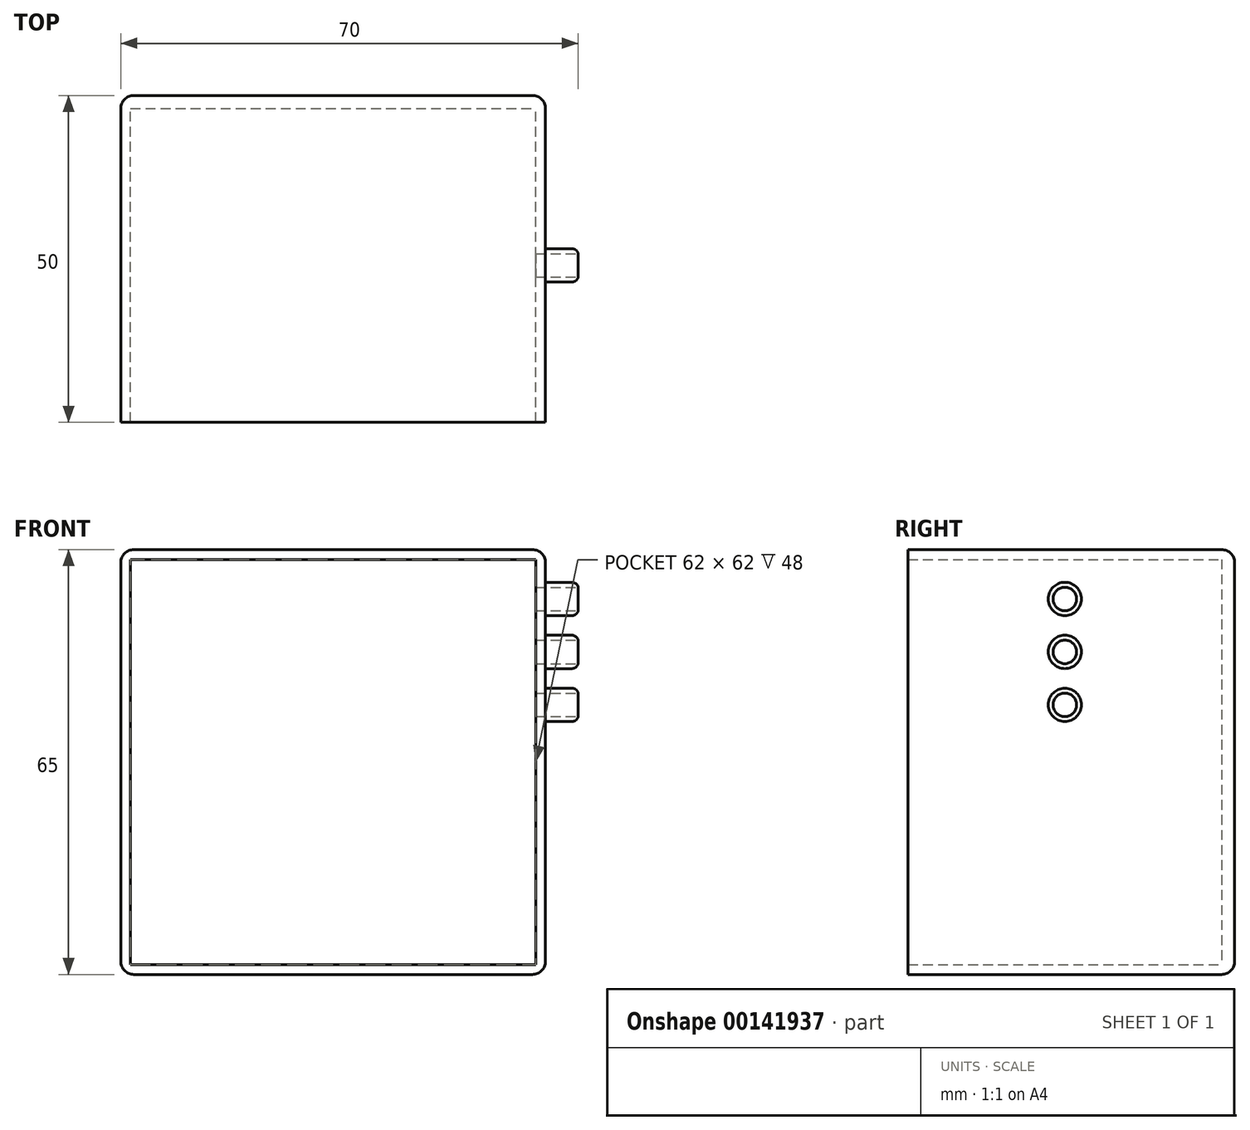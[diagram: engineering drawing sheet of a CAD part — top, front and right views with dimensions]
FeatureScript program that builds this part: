
annotation { "Feature Type Name" : "Feature", "Feature Type Description" : "" }
export const myFeature = defineFeature(function(context is Context, id is Id, definition is map)
    precondition{}
    {
        {
            var Q0;
            Q0=qCreatedBy(makeId("Front.planeOp"),FACE);
            var sketch = newSketch(context, id + "F0", { "sketchPlane" : qUnion([Q0])});
            skLineSegment(sketch, "E0.bottom", {"start": v(-31.66, 27.38) * mm, "end": v(30.34, 27.38) * mm});
            skLineSegment(sketch, "E0.top", {"start": v(-31.66, -34.62) * mm, "end": v(30.34, -34.62) * mm});
            skLineSegment(sketch, "E0.left", {"start": v(-31.66, 27.38) * mm, "end": v(-31.66, -34.62) * mm});
            skLineSegment(sketch, "E0.right", {"start": v(30.34, 27.38) * mm, "end": v(30.34, -34.62) * mm});
            skLineSegment(sketch, "E1.bottom", {"start": v(-33.16, 28.88) * mm, "end": v(31.84, 28.88) * mm});
            skLineSegment(sketch, "E1.top", {"start": v(-33.16, -36.12) * mm, "end": v(31.84, -36.12) * mm});
            skLineSegment(sketch, "E1.left", {"start": v(-33.16, 28.88) * mm, "end": v(-33.16, -36.12) * mm});
            skLineSegment(sketch, "E1.right", {"start": v(31.84, 28.88) * mm, "end": v(31.84, -36.12) * mm});
            skSolve(sketch);
        }
        {
            var Q0;
            Q0=makeQuery(id+"F0.imprint","IMPRINT",FACE,{"disambiguationData":[TD([[makeQuery(id+"F0.imprint","IMPRINT",EDGE,{"derivedFrom":sQuery(id+"F0.wireOp",EDGE,"E0.bottom")}),-1.0]])]});
            extrude(context, id + "F1", {"entities" : qUnion([Q0]), "depth" : 2 * mm});
        }
        {
            var Q0;
            Q0=makeQuery(id+"F0.imprint","IMPRINT",FACE,{"disambiguationData":[TD([[makeQuery(id+"F0.imprint","IMPRINT",EDGE,{"derivedFrom":sQuery(id+"F0.wireOp",EDGE,"E0.bottom")}),1.0]])]});
            extrude(context, id + "F2", {"entities" : qUnion([Q0]), "operationType" : NewBodyOperationType.ADD, "depth" : 50 * mm});
        }
        {
            var Q0;
            Q0=makeQuery(id+"F2.opExtrude","CAP_EDGE",EDGE,{"disambiguationData":[OSD([sQuery(id+"F0.wireOp",EDGE,"E1.right")])],"isStart":true});
            var Q1;
            Q1=makeQuery(id+"F2.opExtrude","CAP_EDGE",EDGE,{"disambiguationData":[OSD([sQuery(id+"F0.wireOp",EDGE,"E1.bottom")])],"isStart":true});
            var Q2;
            Q2=makeQuery(id+"F2.opExtrude","CAP_EDGE",EDGE,{"disambiguationData":[OSD([sQuery(id+"F0.wireOp",EDGE,"E1.left")])],"isStart":true});
            var Q3;
            Q3=makeQuery(id+"F2.opExtrude","CAP_EDGE",EDGE,{"disambiguationData":[OSD([sQuery(id+"F0.wireOp",EDGE,"E1.top")])],"isStart":true});
            var Q4;
            Q4=makeQuery(id+"F2.opExtrude","SWEPT_EDGE",EDGE,{"disambiguationData":[OSD([sQuery(id+"F0.wireOp",EDGE,"E1.bottom"),sQuery(id+"F0.wireOp",EDGE,"E1.right")])]});
            var Q5;
            Q5=makeQuery(id+"F2.opExtrude","SWEPT_EDGE",EDGE,{"disambiguationData":[OSD([sQuery(id+"F0.wireOp",EDGE,"E1.top"),sQuery(id+"F0.wireOp",EDGE,"E1.right")])]});
            var Q6;
            Q6=makeQuery(id+"F2.opExtrude","SWEPT_EDGE",EDGE,{"disambiguationData":[OSD([sQuery(id+"F0.wireOp",EDGE,"E1.top"),sQuery(id+"F0.wireOp",EDGE,"E1.left")])]});
            var Q7;
            Q7=makeQuery(id+"F2.opExtrude","SWEPT_EDGE",EDGE,{"disambiguationData":[OSD([sQuery(id+"F0.wireOp",EDGE,"E1.bottom"),sQuery(id+"F0.wireOp",EDGE,"E1.left")])]});
            fillet(context, id + "F3", {"entities" : qUnion([Q0, Q1, Q2, Q3, Q4, Q5, Q6, Q7]), "radius" : 2 * mm, "tangentPropagation" : true, "allowEdgeOverflow" : false});
        }
        {
            var Q0;
            Q0=makeQuery(id+"F2.opExtrude","SWEPT_FACE",FACE,{"disambiguationData":[OSD([sQuery(id+"F0.wireOp",EDGE,"E1.right")])]});
            var sketch = newSketch(context, id + "F4", { "sketchPlane" : qUnion([Q0])});
            skCircle(sketch, "E2", {"center": v(-26, 21.33) * mm, "radius": 1.8 * mm});
            skPoint(sketch, "E2.centerSnap0", {"position": v(-26, 26.88) * mm});
            skCircle(sketch, "E3", {"center": v(-26, 5.13) * mm, "radius": 1.8 * mm});
            skPoint(sketch, "E3.centerSnap0", {"position": v(-26, -34.12) * mm});
            skCircle(sketch, "E4", {"center": v(-26, 13.23) * mm, "radius": 1.8 * mm});
            skCircle(sketch, "E5", {"center": v(-26, 21.33) * mm, "radius": 2.55 * mm});
            skCircle(sketch, "E6", {"center": v(-26, 13.23) * mm, "radius": 2.55 * mm});
            skCircle(sketch, "E7", {"center": v(-26, 5.13) * mm, "radius": 2.55 * mm});
            skSolve(sketch);
        }
        {
            var Q0;
            Q0=makeQuery(id+"F4.imprint","IMPRINT",FACE,{"disambiguationData":[TD([[makeQuery(id+"F4.imprint","IMPRINT",EDGE,{"derivedFrom":sQuery(id+"F4.wireOp",EDGE,"E2")}),1.0]])]});
            extrude(context, id + "F5", {"entities" : qUnion([Q0]), "operationType" : NewBodyOperationType.REMOVE, "oppositeDirection" : true, "depth" : 25 * mm});
        }
        {
            var Q0;
            Q0=makeQuery(id+"F4.imprint","IMPRINT",FACE,{"disambiguationData":[TD([[makeQuery(id+"F4.imprint","IMPRINT",EDGE,{"derivedFrom":sQuery(id+"F4.wireOp",EDGE,"E4")}),1.0]])]});
            var Q1;
            Q1=makeQuery(id+"F4.imprint","IMPRINT",FACE,{"disambiguationData":[TD([[makeQuery(id+"F4.imprint","IMPRINT",EDGE,{"derivedFrom":sQuery(id+"F4.wireOp",EDGE,"E3")}),1.0]])]});
            extrude(context, id + "F6", {"entities" : qUnion([Q0, Q1]), "operationType" : NewBodyOperationType.REMOVE, "oppositeDirection" : true, "depth" : 25 * mm});
        }
        {
            var Q0;
            Q0=makeQuery(id+"F4.imprint","IMPRINT",FACE,{"disambiguationData":[TD([[makeQuery(id+"F4.imprint","IMPRINT",EDGE,{"derivedFrom":sQuery(id+"F4.wireOp",EDGE,"E2")}),-1.0]])]});
            var Q1;
            Q1=makeQuery(id+"F4.imprint","IMPRINT",FACE,{"disambiguationData":[TD([[makeQuery(id+"F4.imprint","IMPRINT",EDGE,{"derivedFrom":sQuery(id+"F4.wireOp",EDGE,"E4")}),-1.0]])]});
            var Q2;
            Q2=makeQuery(id+"F4.imprint","IMPRINT",FACE,{"disambiguationData":[TD([[makeQuery(id+"F4.imprint","IMPRINT",EDGE,{"derivedFrom":sQuery(id+"F4.wireOp",EDGE,"E3")}),-1.0]])]});
            extrude(context, id + "F7", {"entities" : qUnion([Q0, Q1, Q2]), "operationType" : NewBodyOperationType.ADD, "depth" : 5 * mm});
        }
        {
            var Q0;
            Q0=makeQuery(id+"F7.opExtrude","CAP_EDGE",EDGE,{"disambiguationData":[OSD([sQuery(id+"F4.wireOp",EDGE,"E5")])],"isStart":false});
            var Q1;
            Q1=makeQuery(id+"F7.opExtrude","CAP_EDGE",EDGE,{"disambiguationData":[OSD([sQuery(id+"F4.wireOp",EDGE,"E6")])],"isStart":false});
            var Q2;
            Q2=makeQuery(id+"F7.opExtrude","CAP_EDGE",EDGE,{"disambiguationData":[OSD([sQuery(id+"F4.wireOp",EDGE,"E7")])],"isStart":false});
            fillet(context, id + "F8", {"entities" : qUnion([Q0, Q1, Q2]), "radius" : 1 * mm, "tangentPropagation" : true, "allowEdgeOverflow" : false});
        }
    });
